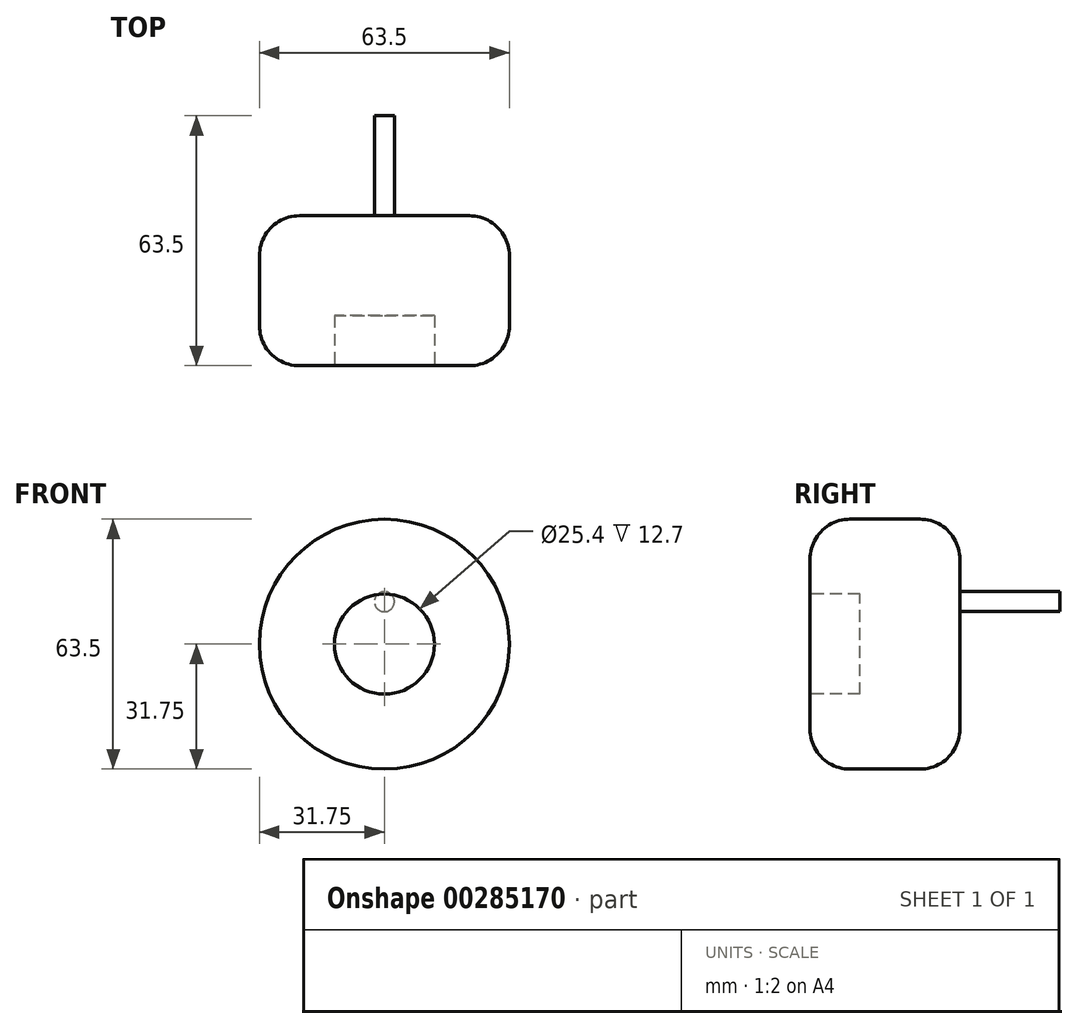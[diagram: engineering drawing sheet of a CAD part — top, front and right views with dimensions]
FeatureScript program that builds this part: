
annotation { "Feature Type Name" : "Feature", "Feature Type Description" : "" }
export const myFeature = defineFeature(function(context is Context, id is Id, definition is map)
    precondition{}
    {
        {
            var Q0;
            Q0=qCreatedBy(makeId("Front.planeOp"),FACE);
            var sketch = newSketch(context, id + "F0", { "sketchPlane" : qUnion([Q0])});
            skCircle(sketch, "E0", {"center": v(0, 0) * mm, "radius": 31.75 * mm});
            skSolve(sketch);
        }
        {
            var Q0;
            Q0=makeQuery(id+"F0.imprint","IMPRINT",FACE,{"disambiguationData":[TD([[makeQuery(id+"F0.imprint","IMPRINT",EDGE,{"derivedFrom":sQuery(id+"F0.wireOp",EDGE,"E0")}),1.0]])]});
            extrude(context, id + "F1", {"entities" : qUnion([Q0]), "depth" : 38.1 * mm});
        }
        {
            var Q0;
            Q0=makeQuery(id+"F1.opExtrude","CAP_EDGE",EDGE,{"disambiguationData":[OSD([sQuery(id+"F0.wireOp",EDGE,"E0")])],"isStart":false});
            var Q1;
            Q1=makeQuery(id+"F1.opExtrude","CAP_EDGE",EDGE,{"disambiguationData":[OSD([sQuery(id+"F0.wireOp",EDGE,"E0")])],"isStart":true});
            fillet(context, id + "F2", {"entities" : qUnion([Q0, Q1]), "radius" : 10.16 * mm, "tangentPropagation" : true, "allowEdgeOverflow" : false});
        }
        {
            var Q0;
            Q0=makeQuery(id+"F1.opExtrude","CAP_FACE",FACE,{"disambiguationData":[OSD([sQuery(id+"F0.wireOp",EDGE,"E0")])],"isStart":true});
            extrude(context, id + "F3", {"entities" : qUnion([Q0]), "operationType" : NewBodyOperationType.ADD, "oppositeDirection" : true, "depth" : 12.7 * mm});
        }
        {
            var Q0;
            Q0=makeQuery(id+"F1.opExtrude","CAP_FACE",FACE,{"disambiguationData":[OSD([sQuery(id+"F0.wireOp",EDGE,"E0")])],"isStart":false});
            var sketch = newSketch(context, id + "F4", { "sketchPlane" : qUnion([Q0])});
            skCircle(sketch, "E1", {"center": v(0, 0) * mm, "radius": 12.7 * mm});
            skSolve(sketch);
        }
        {
            var Q0;
            Q0=makeQuery(id+"F4.imprint","IMPRINT",FACE,{"disambiguationData":[TD([[makeQuery(id+"F4.imprint","IMPRINT",EDGE,{"derivedFrom":sQuery(id+"F4.wireOp",EDGE,"E1")}),1.0]])]});
            extrude(context, id + "F5", {"entities" : qUnion([Q0]), "operationType" : NewBodyOperationType.REMOVE, "oppositeDirection" : true, "depth" : 12.7 * mm});
        }
        {
            var Q0;
            Q0=makeQuery(id+"F1.opExtrude","CAP_FACE",FACE,{"disambiguationData":[OSD([sQuery(id+"F0.wireOp",EDGE,"E0")])],"isStart":true});
            var sketch = newSketch(context, id + "F6", { "sketchPlane" : qUnion([Q0])});
            skLineSegment(sketch, "E2", {"start": v(0, 0) * mm, "end": v(0, 21.59) * mm, "construction": true});
            skCircle(sketch, "E3", {"center": v(0, 10.8) * mm, "radius": 2.54 * mm});
            skSolve(sketch);
        }
        {
            var Q0;
            Q0=makeQuery(id+"F6.imprint","IMPRINT",FACE,{"disambiguationData":[TD([[makeQuery(id+"F6.imprint","IMPRINT",EDGE,{"derivedFrom":sQuery(id+"F6.wireOp",EDGE,"E3")}),1.0]])]});
            extrude(context, id + "F7", {"entities" : qUnion([Q0]), "operationType" : NewBodyOperationType.ADD, "depth" : 25.4 * mm});
        }
    });
